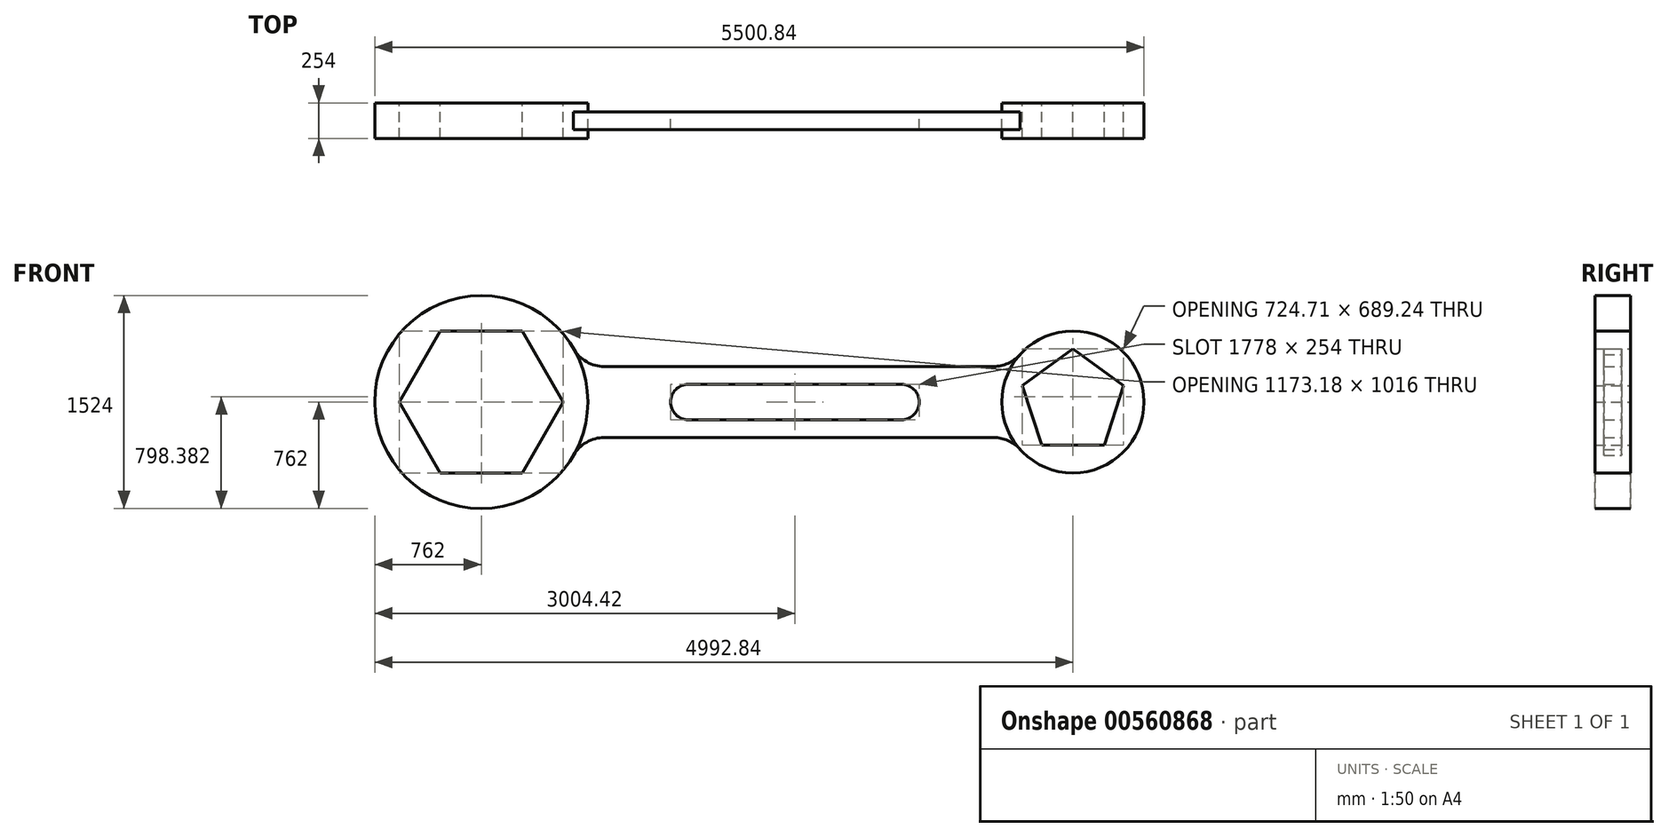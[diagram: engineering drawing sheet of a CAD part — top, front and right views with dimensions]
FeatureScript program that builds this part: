
annotation { "Feature Type Name" : "Feature", "Feature Type Description" : "" }
export const myFeature = defineFeature(function(context is Context, id is Id, definition is map)
    precondition{}
    {
        {
            var Q0;
            Q0=qCreatedBy(makeId("Front.planeOp"),FACE);
            var sketch = newSketch(context, id + "F0", { "sketchPlane" : qUnion([Q0])});
            skCircle(sketch, "E0", {"center": v(0, 0) * mm, "radius": 762 * mm});
            skCircle(sketch, "E1", {"center": v(4230.84, 0) * mm, "radius": 508 * mm});
            skPoint(sketch, "E2.orphan", {"position": v(3131.42, 0) * mm});
            skLineSegment(sketch, "E3", {"start": v(2242.42, 127) * mm, "end": v(1480.42, 127) * mm});
            skLineSegment(sketch, "E4", {"start": v(1480.42, -127) * mm, "end": v(3004.42, -127) * mm});
            skLineSegment(sketch, "E5", {"start": v(3004.42, 127) * mm, "end": v(2242.42, 127) * mm});
            skLineSegment(sketch, "E6", {"start": v(2242.42, -254) * mm, "end": v(879.88, -254) * mm});
            skLineSegment(sketch, "E7", {"start": v(2242.42, -254) * mm, "end": v(3662.88, -254) * mm});
            skLineSegment(sketch, "E8", {"start": v(2242.42, 254) * mm, "end": v(879.88, 254) * mm});
            skLineSegment(sketch, "E9", {"start": v(2242.42, 254) * mm, "end": v(3662.88, 254) * mm});
            skPoint(sketch, "E10.endSnap0", {"position": v(1480.42, -254) * mm});
            skArc(sketch, "E11", {"start": v(1480.42, 127) * mm, "mid": v(1353.42, 0) * mm, "end": v(1480.42, -127) * mm});
            skArc(sketch, "E12", {"start": v(879.88, -254) * mm, "mid": v(752.88, -288.03) * mm, "end": v(659.91, -381) * mm});
            skPoint(sketch, "E13.orphan", {"position": v(1353.42, -127) * mm});
            skArc(sketch, "E14", {"start": v(3004.42, -127) * mm, "mid": v(3131.42, 0) * mm, "end": v(3004.42, 127) * mm});
            skPoint(sketch, "E15.orphan", {"position": v(3131.42, 127) * mm});
            skArc(sketch, "E16", {"start": v(659.91, 381) * mm, "mid": v(752.88, 288.03) * mm, "end": v(879.88, 254) * mm});
            skArc(sketch, "E17", {"start": v(3662.88, 254) * mm, "mid": v(3766.57, 276.13) * mm, "end": v(3852.2, 338.67) * mm});
            skArc(sketch, "E18", {"start": v(3852.2, -338.67) * mm, "mid": v(3766.57, -276.13) * mm, "end": v(3662.88, -254) * mm});
            skPoint(sketch, "E19.start.orphan", {"position": v(1353.42, 127) * mm});
            skCircle(sketch, "E20.cCircle", {"center": v(0, 0) * mm, "radius": 508 * mm, "construction": true});
            skLineSegment(sketch, "E20.0", {"start": v(293.3, -508) * mm, "end": v(-293.3, -508) * mm});
            skLineSegment(sketch, "E20.1", {"start": v(-293.3, -508) * mm, "end": v(-586.59, 0) * mm});
            skLineSegment(sketch, "E20.2", {"start": v(-586.59, 0) * mm, "end": v(-293.3, 508) * mm});
            skLineSegment(sketch, "E20.3", {"start": v(-293.3, 508) * mm, "end": v(293.3, 508) * mm});
            skLineSegment(sketch, "E20.4", {"start": v(293.3, 508) * mm, "end": v(586.59, 0) * mm});
            skLineSegment(sketch, "E20.5", {"start": v(586.59, 0) * mm, "end": v(293.3, -508) * mm});
            skPoint(sketch, "E20.0.midPoint", {"position": v(0, -508) * mm});
            skCircle(sketch, "E21.cCircle", {"center": v(4230.84, 0) * mm, "radius": 308.24 * mm, "construction": true});
            skLineSegment(sketch, "E21.0", {"start": v(4454.79, -308.24) * mm, "end": v(4006.9, -308.24) * mm});
            skLineSegment(sketch, "E21.1", {"start": v(4006.9, -308.24) * mm, "end": v(3868.49, 117.74) * mm});
            skLineSegment(sketch, "E21.2", {"start": v(3868.49, 117.74) * mm, "end": v(4230.84, 381) * mm});
            skLineSegment(sketch, "E21.3", {"start": v(4230.84, 381) * mm, "end": v(4593.2, 117.74) * mm});
            skLineSegment(sketch, "E21.4", {"start": v(4593.2, 117.74) * mm, "end": v(4454.79, -308.24) * mm});
            skPoint(sketch, "E21.0.midPoint", {"position": v(4230.84, -308.24) * mm});
            skPoint(sketch, "E22.orphan", {"position": v(718.42, -254) * mm});
            skSolve(sketch);
        }
        {
            var Q0;
            Q0=makeQuery(id+"F0.imprint","IMPRINT",FACE,{"disambiguationData":[TD([[makeQuery(id+"F0.imprint","IMPRINT",EDGE,{"derivedFrom":sQuery(id+"F0.wireOp",EDGE,"E20.0")}),1.0]])]});
            extrude(context, id + "F1", {"entities" : qUnion([Q0]), "depth" : 254 * mm, "offsetDistance" : 25.4 * mm, "symmetric" : true});
        }
        {
            var Q0;
            Q0=makeQuery(id+"F0.imprint","IMPRINT",FACE,{"disambiguationData":[TD([[makeQuery(id+"F0.imprint","IMPRINT",EDGE,{"derivedFrom":sQuery(id+"F0.wireOp",EDGE,"E21.0")}),1.0]])]});
            extrude(context, id + "F2", {"entities" : qUnion([Q0]), "depth" : 254 * mm, "offsetDistance" : 25.4 * mm, "symmetric" : true});
        }
        {
            var Q0;
            Q0=makeQuery(id+"F0.imprint","IMPRINT",FACE,{"disambiguationData":[TD([[makeQuery(id+"F0.imprint","IMPRINT",EDGE,{"derivedFrom":sQuery(id+"F0.wireOp",EDGE,"E3")}),-1.0]])]});
            extrude(context, id + "F3", {"entities" : qUnion([Q0]), "depth" : 127 * mm, "offsetDistance" : 25.4 * mm, "symmetric" : true});
        }
    });
